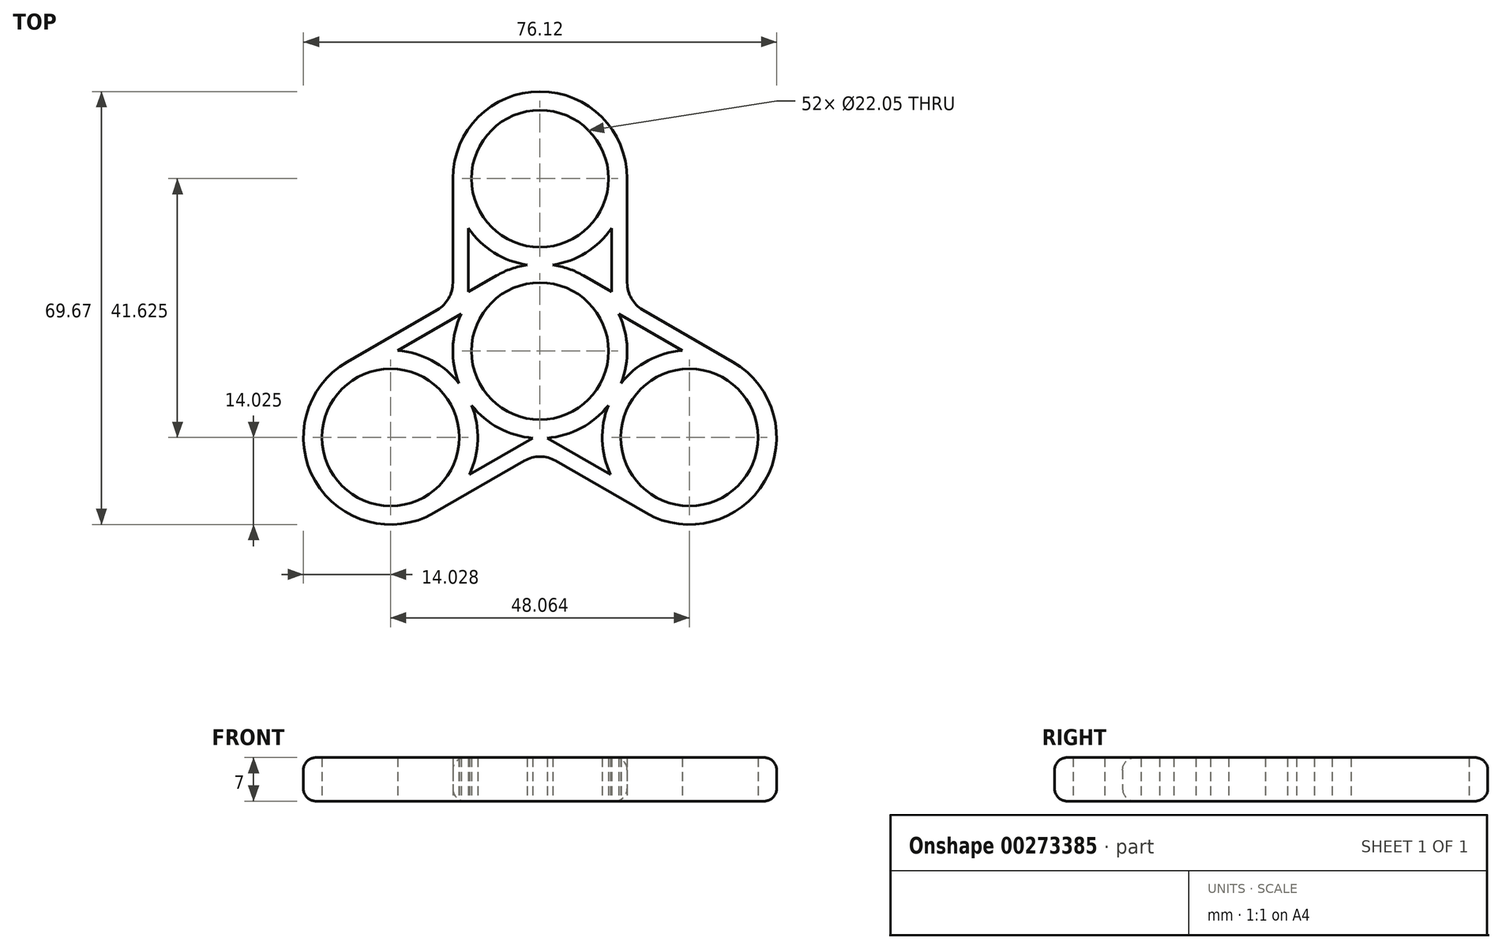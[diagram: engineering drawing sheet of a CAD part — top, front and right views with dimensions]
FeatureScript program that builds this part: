
annotation { "Feature Type Name" : "Feature", "Feature Type Description" : "" }
export const myFeature = defineFeature(function(context is Context, id is Id, definition is map)
    precondition{}
    {
        {
            var Q0;
            Q0=qCreatedBy(makeId("Top.planeOp"),FACE);
            var sketch = newSketch(context, id + "F0", { "sketchPlane" : qUnion([Q0])});
            skCircle(sketch, "E0", {"center": v(0, 0) * mm, "radius": 11.03 * mm});
            skCircle(sketch, "E1", {"center": v(0, 27.75) * mm, "radius": 11.03 * mm});
            skArc(sketch, "E2", {"start": v(2.05, 13.88) * mm, "mid": v(7.4, 15.83) * mm, "end": v(11.52, 19.76) * mm});
            skArc(sketch, "E3", {"start": v(-2.05, 13.88) * mm, "mid": v(-4.61, 13.25) * mm, "end": v(-7.01, 12.15) * mm});
            skLineSegment(sketch, "E4", {"start": v(-14.02, 27.75) * mm, "end": v(-14.02, 10.98) * mm});
            skLineSegment(sketch, "E5", {"start": v(-11.52, 9.54) * mm, "end": v(-11.52, 19.76) * mm});
            skArc(sketch, "E6.trimOffspring", {"start": v(-11.52, 19.76) * mm, "mid": v(-7.4, 15.83) * mm, "end": v(-2.05, 13.88) * mm});
            skLineSegment(sketch, "E7.MirrorCS", {"start": v(11.52, 9.54) * mm, "end": v(11.52, 19.76) * mm});
            skLineSegment(sketch, "E8.MirrorCS", {"start": v(14.02, 27.75) * mm, "end": v(14.02, 10.98) * mm});
            skArc(sketch, "E9.trimOffspring", {"start": v(14.02, 27.75) * mm, "mid": v(0, 41.77) * mm, "end": v(-14.02, 27.75) * mm});
            skArc(sketch, "E10.1.0", {"start": v(-11.35, -19.86) * mm, "mid": v(-10.01, -14.32) * mm, "end": v(-11, -8.7) * mm});
            skArc(sketch, "E10.1.1", {"start": v(-31.04, -1.73) * mm, "mid": v(-36.18, -20.89) * mm, "end": v(-17.02, -26.02) * mm});
            skArc(sketch, "E10.1.2", {"start": v(-13.04, -5.17) * mm, "mid": v(-17.4, -1.51) * mm, "end": v(-22.87, 0.1) * mm});
            skCircle(sketch, "E10.1.3", {"center": v(-24.03, -13.87) * mm, "radius": 11.03 * mm});
            skLineSegment(sketch, "E10.1.4", {"start": v(-12.68, 5.98) * mm, "end": v(-22.87, 0.1) * mm});
            skLineSegment(sketch, "E10.1.5", {"start": v(-31.04, -1.73) * mm, "end": v(-16.52, 6.65) * mm});
            skLineSegment(sketch, "E10.1.6", {"start": v(-1.16, -13.98) * mm, "end": v(-11.35, -19.86) * mm});
            skLineSegment(sketch, "E10.1.7", {"start": v(-17.02, -26.02) * mm, "end": v(-2.5, -17.64) * mm});
            skArc(sketch, "E10.2.0", {"start": v(22.87, 0.1) * mm, "mid": v(17.4, -1.51) * mm, "end": v(13.04, -5.17) * mm});
            skArc(sketch, "E10.2.1", {"start": v(17.02, -26.02) * mm, "mid": v(36.18, -20.89) * mm, "end": v(31.04, -1.73) * mm});
            skArc(sketch, "E10.2.2", {"start": v(11, -8.7) * mm, "mid": v(10.01, -14.32) * mm, "end": v(11.35, -19.86) * mm});
            skCircle(sketch, "E10.2.3", {"center": v(24.03, -13.88) * mm, "radius": 11.03 * mm});
            skLineSegment(sketch, "E10.2.4", {"start": v(1.16, -13.98) * mm, "end": v(11.35, -19.86) * mm});
            skLineSegment(sketch, "E10.2.5", {"start": v(17.02, -26.02) * mm, "end": v(2.5, -17.64) * mm});
            skLineSegment(sketch, "E10.2.6", {"start": v(12.68, 5.98) * mm, "end": v(22.87, 0.1) * mm});
            skLineSegment(sketch, "E10.2.7", {"start": v(31.04, -1.73) * mm, "end": v(16.52, 6.65) * mm});
            skLineSegment(sketch, "E11.trimOffspring", {"start": v(11.52, 9.54) * mm, "end": v(7.01, 12.15) * mm});
            skPoint(sketch, "E12.trimOffspring.end.orphan", {"position": v(14.02, 0) * mm});
            skPoint(sketch, "E13.orphan", {"position": v(11.52, 8) * mm});
            skArc(sketch, "E14.trimOffspring", {"start": v(7.01, 12.15) * mm, "mid": v(4.61, 13.25) * mm, "end": v(2.05, 13.88) * mm});
            skArc(sketch, "E15.trimOffspring", {"start": v(13.04, -5.17) * mm, "mid": v(14.02, 0.45) * mm, "end": v(12.68, 5.98) * mm});
            skArc(sketch, "E16.trimOffspring", {"start": v(-11, -8.7) * mm, "mid": v(-6.62, -12.36) * mm, "end": v(-1.16, -13.98) * mm});
            skArc(sketch, "E17.trimOffspring", {"start": v(-12.68, 5.98) * mm, "mid": v(-14.02, 0.45) * mm, "end": v(-13.04, -5.17) * mm});
            skLineSegment(sketch, "E18.trimOffspring", {"start": v(-11.52, 9.54) * mm, "end": v(-7.01, 12.15) * mm});
            skPoint(sketch, "E19.orphan", {"position": v(-11.52, 8) * mm});
            skPoint(sketch, "E20.trimOffspring.end.orphan", {"position": v(-14.02, 0) * mm});
            skPoint(sketch, "E21.orphan", {"position": v(-7.01, -12.15) * mm});
            skPoint(sketch, "E22.orphan", {"position": v(7.01, -12.15) * mm});
            skArc(sketch, "E23.trimOffspring", {"start": v(1.16, -13.98) * mm, "mid": v(6.62, -12.36) * mm, "end": v(11, -8.7) * mm});
            skPoint(sketch, "E24.visualSharp", {"position": v(-14.02, 8.1) * mm});
            skArc(sketch, "E24.filletArc", {"start": v(-16.53, 6.65) * mm, "mid": v(-14.7, 8.48) * mm, "end": v(-14.02, 10.98) * mm});
            skPoint(sketch, "E25.visualSharp", {"position": v(14.02, 8.1) * mm});
            skArc(sketch, "E25.filletArc", {"start": v(14.03, 10.98) * mm, "mid": v(14.7, 8.48) * mm, "end": v(16.52, 6.65) * mm});
            skPoint(sketch, "E26.visualSharp", {"position": v(0, -16.2) * mm});
            skArc(sketch, "E26.filletArc", {"start": v(2.5, -17.64) * mm, "mid": v(0, -16.97) * mm, "end": v(-2.5, -17.64) * mm});
            skLineSegment(sketch, "E27", {"start": v(-7.73, -20.66) * mm, "end": v(7.73, -20.66) * mm, "construction": true});
            skSolve(sketch);
        }
        {
            var Q0;
            Q0=makeQuery(id+"F0.imprint","IMPRINT",FACE,{"disambiguationData":[TD([[makeQuery(id+"F0.imprint","IMPRINT",EDGE,{"derivedFrom":sQuery(id+"F0.wireOp",EDGE,"E0")}),-1.0]])]});
            extrude(context, id + "F1", {"entities" : qUnion([Q0]), "depth" : 7 * mm});
        }
        {
            var Q0;
            Q0=makeQuery(id+"F1.opExtrude","CAP_EDGE",EDGE,{"disambiguationData":[OSD([sQuery(id+"F0.wireOp",EDGE,"E10.1.1")])],"isStart":false});
            var Q1;
            Q1=makeQuery(id+"F1.opExtrude","CAP_EDGE",EDGE,{"disambiguationData":[OSD([sQuery(id+"F0.wireOp",EDGE,"E10.1.7")])],"isStart":false});
            var Q2;
            Q2=makeQuery(id+"F1.opExtrude","CAP_EDGE",EDGE,{"disambiguationData":[OSD([sQuery(id+"F0.wireOp",EDGE,"E26.filletArc")])],"isStart":false});
            var Q3;
            Q3=makeQuery(id+"F1.opExtrude","CAP_EDGE",EDGE,{"disambiguationData":[OSD([sQuery(id+"F0.wireOp",EDGE,"E10.2.5")])],"isStart":false});
            var Q4;
            Q4=makeQuery(id+"F1.opExtrude","CAP_EDGE",EDGE,{"disambiguationData":[OSD([sQuery(id+"F0.wireOp",EDGE,"E10.2.1")])],"isStart":false});
            var Q5;
            Q5=makeQuery(id+"F1.opExtrude","CAP_EDGE",EDGE,{"disambiguationData":[OSD([sQuery(id+"F0.wireOp",EDGE,"E10.2.7")])],"isStart":false});
            var Q6;
            Q6=makeQuery(id+"F1.opExtrude","CAP_EDGE",EDGE,{"disambiguationData":[OSD([sQuery(id+"F0.wireOp",EDGE,"E25.filletArc")])],"isStart":false});
            var Q7;
            Q7=makeQuery(id+"F1.opExtrude","CAP_EDGE",EDGE,{"disambiguationData":[OSD([sQuery(id+"F0.wireOp",EDGE,"E10.1.5")])],"isStart":false});
            var Q8;
            Q8=makeQuery(id+"F1.opExtrude","CAP_EDGE",EDGE,{"disambiguationData":[OSD([sQuery(id+"F0.wireOp",EDGE,"E24.filletArc")])],"isStart":false});
            var Q9;
            Q9=makeQuery(id+"F1.opExtrude","CAP_EDGE",EDGE,{"disambiguationData":[OSD([sQuery(id+"F0.wireOp",EDGE,"E9.trimOffspring")])],"isStart":false});
            var Q10;
            Q10=makeQuery(id+"F1.opExtrude","CAP_EDGE",EDGE,{"disambiguationData":[OSD([sQuery(id+"F0.wireOp",EDGE,"E8.MirrorCS")])],"isStart":false});
            var Q11;
            Q11=makeQuery(id+"F1.opExtrude","CAP_EDGE",EDGE,{"disambiguationData":[OSD([sQuery(id+"F0.wireOp",EDGE,"E10.1.5")])],"isStart":true});
            var Q12;
            Q12=makeQuery(id+"F1.opExtrude","CAP_EDGE",EDGE,{"disambiguationData":[OSD([sQuery(id+"F0.wireOp",EDGE,"E10.1.1")])],"isStart":true});
            fillet(context, id + "F2", {"entities" : qUnion([Q0, Q1, Q2, Q3, Q4, Q5, Q6, Q7, Q8, Q9, Q10, Q11, Q12]), "radius" : 2 * mm, "tangentPropagation" : true, "allowEdgeOverflow" : false});
        }
    });
